# Revit family: VTi.933.I_Пресс-тройник с наруж резьбой_Нерж_VALTEC
name_source: partatom
category: Обобщенные модели
units: mm (PartAtom-declared; Revit-internal decimal feet)

## family parameters
Всегда вертикально = Да
Может служить основой для арматурных стержней = Нет
На основе рабочей плоскости = Нет
Общий = Нет
При загрузке вырезать с полостями = Нет
Размер круглого соединителя = Использовать диаметр
Сохранять ориентацию аннотаций = Нет
Тип детали = Нормальный
Точка принадлежности помещению = Нет

## types (14) — shared parameters
ADSK_Единица измерения = шт.
ADSK_Количество = 1
ADSK_Материал = Сталь, нержавеющая - VALTEC
LT = VTi.933.I_Пресс-тройник с наруж резьбой_Нерж_VALTEC
zero-valued in all types: Отметка по умолчанию

## type names (no varying parameters)
- Фитинг из нержавеющей стали - пресс-тройник с наружной резьбой 15 мм х 1/2"
- Фитинг из нержавеющей стали - пресс-тройник с наружной резьбой 18 мм х 1/2"
- Фитинг из нержавеющей стали - пресс-тройник с наружной резьбой 18 мм х 3/4"
- Фитинг из нержавеющей стали - пресс-тройник с наружной резьбой 22 мм х 1/2"
- Фитинг из нержавеющей стали - пресс-тройник с наружной резьбой 22 мм х 3/4"
- Фитинг из нержавеющей стали - пресс-тройник с наружной резьбой 28 мм х 1/2"
- Фитинг из нержавеющей стали - пресс-тройник с наружной резьбой 28 мм х 3/4"
- Фитинг из нержавеющей стали - пресс-тройник с наружной резьбой 28 мм х 1"
- Фитинг из нержавеющей стали - пресс-тройник с наружной резьбой 35 мм х 1"
- Фитинг из нержавеющей стали - пресс-тройник с наружной резьбой 35 мм х 1 1/4"
- Фитинг из нержавеющей стали - пресс-тройник с наружной резьбой 42 мм х 1"
- Фитинг из нержавеющей стали - пресс-тройник с наружной резьбой 42 мм х 1 1/4"
- Фитинг из нержавеющей стали - пресс-тройник с наружной резьбой 54 мм х 1"
- Фитинг из нержавеющей стали - пресс-тройник с наружной резьбой 54 мм х 1 1/4"
